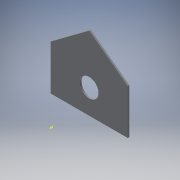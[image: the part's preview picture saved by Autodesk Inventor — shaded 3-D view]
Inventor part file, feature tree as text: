
AUTODESK INVENTOR PART (.ipt)
format: ipt  version: 2017 (Build 210142000, 142)  size: 145,408 bytes
history: native  units: in
note: dims shown in document units (in); Inventor stores cm internally (conversion verified against a paired STEP export)
features: sketch x11, extrude x6
ambient origin geometry x8: Origin, YZ Plane, XZ Plane, XY Plane, X Axis, Y Axis, Z Axis, Center Point
bodies: Solid1 (feature_tree)
feature tree (17):
  sketch  "Sketch1"  dims[d0=13.189in d1=17.7165in]
  extrude  "Extrusion1"  Depth=17.7165in
  extrude  "Extrusion2"  Depth=0.2756in TaperAngle=0.0deg
  extrude  "Extrusion3"  Depth=12.7953in
  sketch  "Sketch6"  dims[d11=12.0256in d12=0.0in d25=1.5748in]
  sketch  "Sketch7"  dims[d26=3.1496in d27=5.1181in]
  sketch  "Sketch8"  dims[d28=0.3937in d29=0.0in]
  sketch  "Sketch9"  dims[d30=2.5591in]
  extrude  "Extrusion6"  Depth=12.7953in
  extrude  "Extrusion7"  Depth=1.5748in
  extrude  "Extrusion10"  Depth=5.1181in
  sketch  "Sketch2"  dims[d2=6.5945in d3=0.2756in d4=0.0in]
  sketch  "Sketch3"  dims[d5=6.5945in d6=12.7953in]
  sketch  "Sketch5"  dims[d7=6.5369in d8=0.0in d10=12.7953in]
  sketch  "Sketch12"  dims[d31=1.5945in]
  sketch  "Sketch13"  dims[d32=1.5945in]
  sketch  "Sketch18"  dims[d33=0.3937in d34=0.0in d43=13.189in d44=5.1181in d45=0.3937in d46=0.0in]
